# Revit family: PT, PS, 129, 159, 189, 219, 249, 1212, 1512,1215,1515,1815,1218,1518,1818
name_source: partatom
category: Windows
revit_build: Autodesk Revit LT 2016 (Build: 20150220_1215(x64)
units: mm (PartAtom-declared; Revit-internal decimal feet)

## family parameters
Always vertical = Yes
Cut with Voids When Loaded = No
Host = Wall
OmniClass Number = 23.30.20.00
OmniClass Title = Windows
Room Calculation Point = No
Shared = No

## types (13) — shared parameters
Aluminium anodized = Aluminium
Default Sill Height = 914 mm
Glazing = Glass
Manufacturer = Robmeg
Plaster = 5 mm  [stored 0.0164042 ft]
Rough Height = 1219 mm
URL = http://www.robmeg.co.za
Wall Closure = By host

## per-type parameters (varying)
| type | Bottom glazing thickness | Bottom mullion | Centre vert mullion | Description | Height | Model | Side Glazing thickness | Side hung | Top hung | Width |
| PT Type- 129 | 4 mm  [stored 0.0131234 ft] | 300 mm | 610 mm  [stored 2.00131 ft] | Anodized Aluminium | 910 mm | PT 129 | 4 mm  [stored 0.0131234 ft] | No | Yes | 1210 mm  [stored 3.96982 ft] |
| PT Type- 159 | 4 mm  [stored 0.0131234 ft] | 300 mm | 610 mm  [stored 2.00131 ft] | Anodized Aluminium | 910 mm | PT 159 | 4 mm  [stored 0.0131234 ft] | No | Yes | 1510 mm  [stored 4.95407 ft] |
| PT Type- 189 | 4 mm  [stored 0.0131234 ft] | 300 mm | 905 mm  [stored 2.96916 ft] | Anodized Alumium | 910 mm | PT 189 | 4 mm  [stored 0.0131234 ft] | No | Yes | 1810 mm  [stored 5.93832 ft] |
| PT Type- 219 | 4 mm  [stored 0.0131234 ft] | 300 mm | 905 mm  [stored 2.96916 ft] | Anodized Alumium | 910 mm | PT 219 | 4 mm  [stored 0.0131234 ft] | Yes | No | 2110 mm  [stored 6.92257 ft] |
| PT Type- 249 | 4 mm  [stored 0.0131234 ft] | 300 mm | 905 mm  [stored 2.96916 ft] | Anodized Alumium | 910 mm | PT 249 | 4 mm  [stored 0.0131234 ft] | Yes | No | 2410 mm  [stored 7.90682 ft] |
| PS Type- 1215 | 4 mm  [stored 0.0131234 ft] | 300 mm | 605 mm  [stored 1.98491 ft] | Anodized Aluminium | 1510 mm  [stored 4.95407 ft] | PS 1215 | 4 mm  [stored 0.0131234 ft] | Yes | No | 1210 mm  [stored 3.96982 ft] |
| PS Type-1515 | 4 mm  [stored 0.0131234 ft] | 300 mm | 605 mm  [stored 1.98491 ft] | Anodized Aluminium | 1510 mm  [stored 4.95407 ft] | PS 1515 | 4 mm  [stored 0.0131234 ft] | Yes | No | 1510 mm  [stored 4.95407 ft] |
| PS Type- 1815 | 4 mm  [stored 0.0131234 ft] | 300 mm | 605 mm  [stored 1.98491 ft] | Anodized Aluminium | 1510 mm  [stored 4.95407 ft] | PS 1815 | 4 mm  [stored 0.0131234 ft] | Yes | No | 1810 mm  [stored 5.93832 ft] |
| PS Type- 1218 | 6 mm  [stored 0.019685 ft] | 500 mm  [stored 1.64042 ft] | 605 mm  [stored 1.98491 ft] | Anodized Aluminium | 1510 mm  [stored 4.95407 ft] | PS 1218 | 6 mm  [stored 0.019685 ft] | Yes | No | 1210 mm  [stored 3.96982 ft] |
| PS Type-1518 | 6 mm  [stored 0.019685 ft] | 500 mm  [stored 1.64042 ft] | 605 mm  [stored 1.98491 ft] | Anodized Aluminium | 1510 mm  [stored 4.95407 ft] | PS 1518 | 6 mm  [stored 0.019685 ft] | Yes | No | 1510 mm  [stored 4.95407 ft] |
| PS Type- 1818 | 6 mm  [stored 0.019685 ft] | 500 mm  [stored 1.64042 ft] | 605 mm  [stored 1.98491 ft] | Anodized Aluminium | 1510 mm  [stored 4.95407 ft] | PS 1818 | 6 mm  [stored 0.019685 ft] | Yes | No | 1810 mm  [stored 5.93832 ft] |
| PT Type- 1212 | 4 mm  [stored 0.0131234 ft] | 605 mm  [stored 1.98491 ft] | 610 mm  [stored 2.00131 ft] | Anodized Aluminium | 1210 mm  [stored 3.96982 ft] | PT 1212 | 4 mm  [stored 0.0131234 ft] | No | Yes | 1210 mm  [stored 3.96982 ft] |
| PT Type- 1512 | 4 mm  [stored 0.0131234 ft] | 605 mm  [stored 1.98491 ft] | 610 mm  [stored 2.00131 ft] | Anodized Aluminium | 1210 mm  [stored 3.96982 ft] | PT 1512 | 4 mm  [stored 0.0131234 ft] | No | Yes | 1510 mm  [stored 4.95407 ft] |

note: [stored X ft] marks values corroborated as IEEE doubles in the binary element streams (Revit-internal decimal feet)

## geometry (parser evidence)
native form markers: Sweep x4
no freeform markers — native parametric forms only
